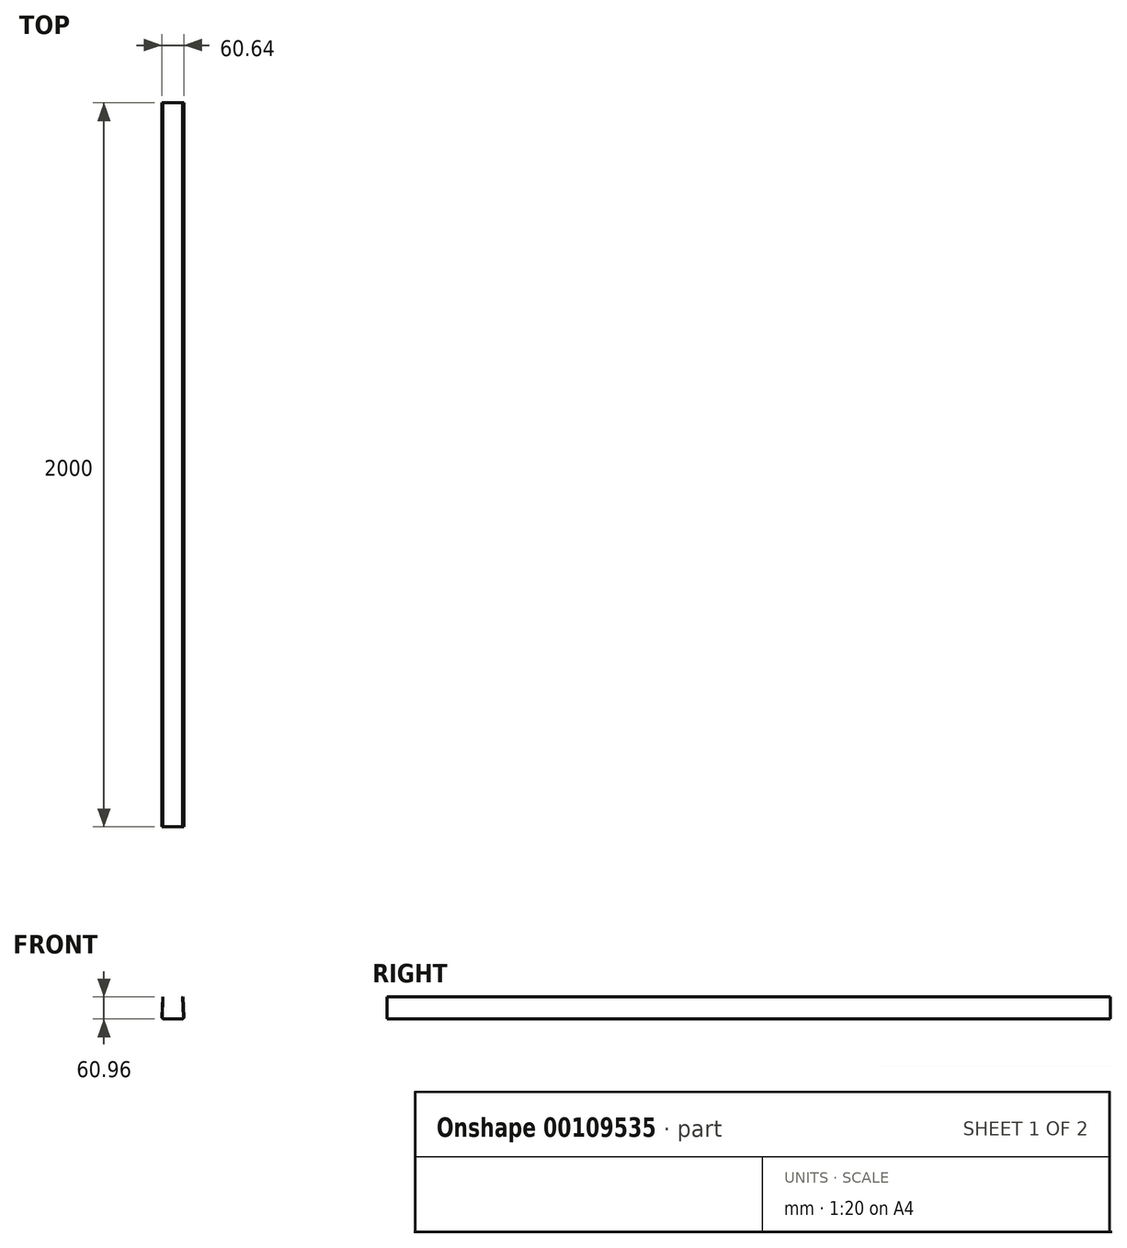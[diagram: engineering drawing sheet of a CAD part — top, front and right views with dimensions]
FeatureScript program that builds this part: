
annotation { "Feature Type Name" : "Feature", "Feature Type Description" : "" }
export const myFeature = defineFeature(function(context is Context, id is Id, definition is map)
    precondition{}
    {
        {
            var Q0;
            Q0=qCreatedBy(makeId("Front.planeOp"),FACE);
            var sketch = newSketch(context, id + "F0", { "sketchPlane" : qUnion([Q0])});
            skLineSegment(sketch, "E0", {"start": v(0, 0) * mm, "end": v(25.32, 0) * mm});
            skLineSegment(sketch, "E1", {"start": v(30.32, 5.17) * mm, "end": v(28.37, 60.96) * mm});
            skLineSegment(sketch, "E2.0", {"start": v(29.32, 5.14) * mm, "end": v(27.39, 60.52) * mm});
            skLineSegment(sketch, "E2.1", {"start": v(0, 1) * mm, "end": v(25.32, 1) * mm});
            skLineSegment(sketch, "E3", {"start": v(27.39, 60.52) * mm, "end": v(28.37, 60.96) * mm});
            skLineSegment(sketch, "E4.MirrorCS", {"start": v(-27.39, 60.52) * mm, "end": v(-28.37, 60.96) * mm});
            skLineSegment(sketch, "E5.MirrorCS", {"start": v(0, 1) * mm, "end": v(-25.32, 1) * mm});
            skLineSegment(sketch, "E6.MirrorCS", {"start": v(-29.32, 5.14) * mm, "end": v(-27.39, 60.52) * mm});
            skLineSegment(sketch, "E7.MirrorCS", {"start": v(-30.32, 5.17) * mm, "end": v(-28.37, 60.96) * mm});
            skLineSegment(sketch, "E8.MirrorCS", {"start": v(0, 0) * mm, "end": v(-25.32, 0) * mm});
            skPoint(sketch, "E9.visualSharp", {"position": v(30.5, 0) * mm});
            skArc(sketch, "E9.filletArc", {"start": v(25.32, 0) * mm, "mid": v(28.92, 1.53) * mm, "end": v(30.32, 5.17) * mm});
            skPoint(sketch, "E10.visualSharp", {"position": v(29.46, 1) * mm});
            skArc(sketch, "E10.filletArc", {"start": v(25.32, 1) * mm, "mid": v(28.2, 2.22) * mm, "end": v(29.32, 5.14) * mm});
            skPoint(sketch, "E11.visualSharp", {"position": v(-29.46, 1) * mm});
            skArc(sketch, "E11.filletArc", {"start": v(-29.32, 5.14) * mm, "mid": v(-28.2, 2.22) * mm, "end": v(-25.32, 1) * mm});
            skPoint(sketch, "E12.visualSharp", {"position": v(-30.5, 0) * mm});
            skArc(sketch, "E12.filletArc", {"start": v(-30.32, 5.17) * mm, "mid": v(-28.92, 1.53) * mm, "end": v(-25.32, 0) * mm});
            skLineSegment(sketch, "E13", {"start": v(28.37, 60.96) * mm, "end": v(16.2, 60.96) * mm, "construction": true});
            skSolve(sketch);
        }
        {
            var Q0;
            Q0=makeQuery(id+"F0.imprint","IMPRINT",FACE,{"disambiguationData":[TD([[makeQuery(id+"F0.imprint","IMPRINT",EDGE,{"derivedFrom":sQuery(id+"F0.wireOp",EDGE,"E0")}),1.0]])]});
            extrude(context, id + "F1", {"entities" : qUnion([Q0]), "oppositeDirection" : true, "depth" : 2000 * mm});
        }
    });
